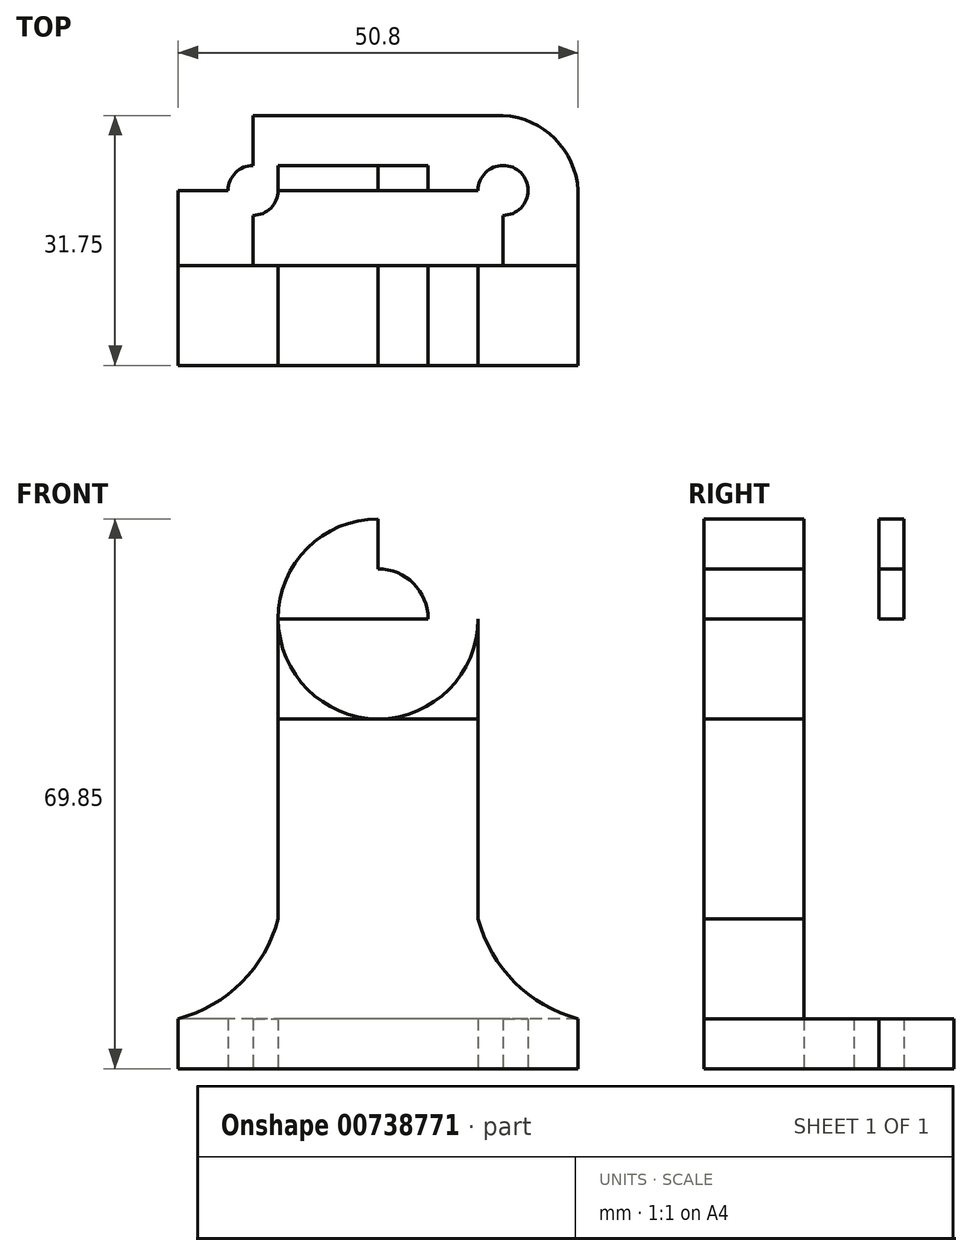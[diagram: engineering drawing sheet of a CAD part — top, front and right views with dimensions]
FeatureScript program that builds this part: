
annotation { "Feature Type Name" : "Feature", "Feature Type Description" : "" }
export const myFeature = defineFeature(function(context is Context, id is Id, definition is map)
    precondition{}
    {
        {
            var Q0;
            Q0=qCreatedBy(makeId("Right.planeOp"),FACE);
            var sketch = newSketch(context, id + "F0", { "sketchPlane" : qUnion([Q0])});
            skLineSegment(sketch, "E0", {"start": v(0, 0) * mm, "end": v(0, 69.85) * mm});
            skLineSegment(sketch, "E1", {"start": v(0, 69.85) * mm, "end": v(25.4, 69.85) * mm});
            skLineSegment(sketch, "E2", {"start": v(25.4, 69.85) * mm, "end": v(25.4, 44.45) * mm});
            skLineSegment(sketch, "E3", {"start": v(25.4, 44.45) * mm, "end": v(12.7, 44.45) * mm});
            skLineSegment(sketch, "E4", {"start": v(12.7, 44.45) * mm, "end": v(12.7, 6.35) * mm});
            skLineSegment(sketch, "E5", {"start": v(12.7, 6.35) * mm, "end": v(31.75, 6.35) * mm});
            skLineSegment(sketch, "E6", {"start": v(31.75, 6.35) * mm, "end": v(31.75, 0) * mm});
            skLineSegment(sketch, "E7", {"start": v(31.75, 0) * mm, "end": v(0, 0) * mm});
            skSolve(sketch);
        }
        {
            var Q0;
            Q0 = qSketchRegion(id + "F0", true);
            extrude(context, id + "F1", {"entities" : qUnion([Q0]), "depth" : 50.8 * mm, "offsetDistance" : 25.4 * mm});
        }
        {
            var Q0;
            Q0=qCreatedBy(makeId("Front.planeOp"),FACE);
            var sketch = newSketch(context, id + "F2", { "sketchPlane" : qUnion([Q0])});
            skLineSegment(sketch, "E8", {"start": v(38.1, 44.45) * mm, "end": v(38.1, 6.35) * mm});
            skLineSegment(sketch, "E9", {"start": v(12.7, 44.45) * mm, "end": v(12.7, 6.35) * mm});
            skLineSegment(sketch, "E10", {"start": v(50.8, 19.05) * mm, "end": v(0, 19.05) * mm});
            skArc(sketch, "E11", {"start": v(38.1, 19.05) * mm, "mid": v(42.73, 10.98) * mm, "end": v(50.8, 6.35) * mm});
            skArc(sketch, "E12", {"start": v(0, 6.35) * mm, "mid": v(8.07, 10.98) * mm, "end": v(12.7, 19.05) * mm});
            skLineSegment(sketch, "E13", {"start": v(38.1, 19.05) * mm, "end": v(38.1, 44.45) * mm});
            skLineSegment(sketch, "E14", {"start": v(38.1, 44.45) * mm, "end": v(50.8, 44.45) * mm});
            skLineSegment(sketch, "E15", {"start": v(50.8, 44.45) * mm, "end": v(50.8, 6.35) * mm});
            skLineSegment(sketch, "E16", {"start": v(12.7, 44.45) * mm, "end": v(0, 44.45) * mm});
            skLineSegment(sketch, "E17", {"start": v(0, 44.45) * mm, "end": v(0, 6.35) * mm});
            skLineSegment(sketch, "E18", {"start": v(38.1, 6.35) * mm, "end": v(38.1, 69.85) * mm});
            skLineSegment(sketch, "E19", {"start": v(38.1, 69.85) * mm, "end": v(50.8, 69.85) * mm});
            skLineSegment(sketch, "E20", {"start": v(50.8, 69.85) * mm, "end": v(50.8, 6.35) * mm});
            skLineSegment(sketch, "E21", {"start": v(12.7, 6.35) * mm, "end": v(12.7, 69.85) * mm});
            skLineSegment(sketch, "E22", {"start": v(12.7, 69.85) * mm, "end": v(0, 69.85) * mm});
            skLineSegment(sketch, "E23", {"start": v(0, 69.85) * mm, "end": v(0, 6.35) * mm});
            skSolve(sketch);
        }
        {
            var Q0;
            Q0 = qSketchRegion(id + "F2", true);
            extrude(context, id + "F3", {"entities" : qUnion([Q0]), "operationType" : NewBodyOperationType.REMOVE, "endBound" : BoundingType.THROUGH_ALL, "oppositeDirection" : true, "depth" : 25.4 * mm, "offsetDistance" : 25.4 * mm});
        }
        {
            var Q0;
            Q0=qCreatedBy(makeId("Front.planeOp"),FACE);
            var sketch = newSketch(context, id + "F4", { "sketchPlane" : qUnion([Q0])});
            skLineSegment(sketch, "E24", {"start": v(25.4, 69.85) * mm, "end": v(25.4, 44.45) * mm});
            skLineSegment(sketch, "E25", {"start": v(38, 57.15) * mm, "end": v(12.6, 57.15) * mm});
            skCircle(sketch, "E26", {"center": v(25.4, 57.15) * mm, "radius": 6.35 * mm});
            skCircle(sketch, "E27", {"center": v(25.4, 57.15) * mm, "radius": 12.7 * mm});
            skLineSegment(sketch, "E28", {"start": v(25.4, 69.85) * mm, "end": v(38.1, 69.85) * mm});
            skLineSegment(sketch, "E29", {"start": v(38.1, 69.85) * mm, "end": v(38.1, 44.45) * mm});
            skLineSegment(sketch, "E30", {"start": v(38.1, 44.45) * mm, "end": v(25.4, 44.45) * mm});
            skLineSegment(sketch, "E31", {"start": v(25.4, 44.45) * mm, "end": v(12.7, 44.45) * mm});
            skLineSegment(sketch, "E32", {"start": v(12.7, 44.45) * mm, "end": v(12.7, 69.85) * mm});
            skLineSegment(sketch, "E33", {"start": v(12.7, 69.85) * mm, "end": v(25.4, 69.85) * mm});
            skSolve(sketch);
        }
        {
            var Q0;
            {var subQ0=sQuery(id+"F4.wireOp",EDGE,"E28");Q0=makeQuery(id+"F4.imprint","IMPRINT",FACE,{"disambiguationData":[TD([[makeQuery(id+"F4.imprint","IMPRINT",EDGE,{"derivedFrom":subQ0}),-1.0]])]});}
            var Q1;
            {var subQ0=sQuery(id+"F4.wireOp",EDGE,"E33");Q1=makeQuery(id+"F4.imprint","IMPRINT",FACE,{"disambiguationData":[TD([[makeQuery(id+"F4.imprint","IMPRINT",EDGE,{"derivedFrom":subQ0}),-1.0]])]});}
            var Q2;
            {var subQ0=sQuery(id+"F4.wireOp",EDGE,"E31");Q2=makeQuery(id+"F4.imprint","IMPRINT",FACE,{"disambiguationData":[TD([[makeQuery(id+"F4.imprint","IMPRINT",EDGE,{"derivedFrom":subQ0}),-1.0]])]});}
            var Q3;
            {var subQ0=sQuery(id+"F4.wireOp",EDGE,"E30");Q3=makeQuery(id+"F4.imprint","IMPRINT",FACE,{"disambiguationData":[TD([[makeQuery(id+"F4.imprint","IMPRINT",EDGE,{"derivedFrom":subQ0}),-1.0]])]});}
            var Q4;
            {var subQ0=sQuery(id+"F4.wireOp",EDGE,"E25");var subQ1=sQuery(id+"F4.wireOp",EDGE,"E24");var subQ2=makeQuery(id+"F4.imprint","INTERSECT",VERTEX,{"derivedFrom":[subQ1,subQ0]});Q4=makeQuery(id+"F4.imprint","IMPRINT",FACE,{"disambiguationData":[TD([[makeQuery(id+"F4.imprint","IMPRINT",EDGE,{"disambiguationData":[TD([[subQ2,-1.0]])],"derivedFrom":subQ1}),-1.0]])]});}
            var Q5;
            {var subQ0=sQuery(id+"F4.wireOp",EDGE,"E25");var subQ1=sQuery(id+"F4.wireOp",EDGE,"E24");var subQ2=makeQuery(id+"F4.imprint","INTERSECT",VERTEX,{"derivedFrom":[subQ1,subQ0]});Q5=makeQuery(id+"F4.imprint","IMPRINT",FACE,{"disambiguationData":[TD([[makeQuery(id+"F4.imprint","IMPRINT",EDGE,{"disambiguationData":[TD([[subQ2,-1.0]])],"derivedFrom":subQ1}),1.0]])]});}
            var Q6;
            {var subQ0=sQuery(id+"F4.wireOp",EDGE,"E26");var subQ1=sQuery(id+"F4.wireOp",EDGE,"E24");var subQ2=makeQuery(id+"F4.imprint","INTERSECT",VERTEX,{"disambiguationData":[OD(0.0)],"derivedFrom":[subQ1,subQ0]});Q6=makeQuery(id+"F4.imprint","IMPRINT",FACE,{"disambiguationData":[TD([[makeQuery(id+"F4.imprint","IMPRINT",EDGE,{"disambiguationData":[TD([[subQ2,-1.0]])],"derivedFrom":subQ1}),1.0]])]});}
            var Q7;
            {var subQ0=sQuery(id+"F4.wireOp",EDGE,"E26");var subQ1=sQuery(id+"F4.wireOp",EDGE,"E24");var subQ2=makeQuery(id+"F4.imprint","INTERSECT",VERTEX,{"disambiguationData":[OD(0.0)],"derivedFrom":[subQ1,subQ0]});Q7=makeQuery(id+"F4.imprint","IMPRINT",FACE,{"disambiguationData":[TD([[makeQuery(id+"F4.imprint","IMPRINT",EDGE,{"disambiguationData":[TD([[subQ2,-1.0]])],"derivedFrom":subQ1}),-1.0]])]});}
            extrude(context, id + "F5", {"entities" : qUnion([Q0, Q1, Q2, Q3, Q4, Q5, Q6, Q7]), "operationType" : NewBodyOperationType.REMOVE, "endBound" : BoundingType.THROUGH_ALL, "oppositeDirection" : true, "depth" : 25.4 * mm, "offsetDistance" : 25.4 * mm});
        }
        {
            var Q0;
            Q0=qCreatedBy(makeId("Front.planeOp"),FACE);
            var sketch = newSketch(context, id + "F6", { "sketchPlane" : qUnion([Q0])});
            skLineSegment(sketch, "E34", {"start": v(12.71, 57.15) * mm, "end": v(38.11, 57.15) * mm});
            skLineSegment(sketch, "E35", {"start": v(12.71, 57.15) * mm, "end": v(12.71, 44.45) * mm});
            skLineSegment(sketch, "E36", {"start": v(12.71, 44.45) * mm, "end": v(38.11, 44.45) * mm});
            skLineSegment(sketch, "E37", {"start": v(38.11, 44.45) * mm, "end": v(38.11, 57.15) * mm});
            skArc(sketch, "E38", {"start": v(12.71, 57.15) * mm, "mid": v(16.43, 48.17) * mm, "end": v(25.41, 44.45) * mm});
            skArc(sketch, "E39", {"start": v(25.41, 44.45) * mm, "mid": v(34.4, 48.17) * mm, "end": v(38.11, 57.15) * mm});
            skSolve(sketch);
        }
        {
            var Q0;
            {var subQ0=sQuery(id+"F6.wireOp",EDGE,"E35");Q0=makeQuery(id+"F6.imprint","IMPRINT",FACE,{"disambiguationData":[TD([[makeQuery(id+"F6.imprint","IMPRINT",EDGE,{"derivedFrom":subQ0}),1.0]])]});}
            var Q1;
            {var subQ0=sQuery(id+"F6.wireOp",EDGE,"E37");Q1=makeQuery(id+"F6.imprint","IMPRINT",FACE,{"disambiguationData":[TD([[makeQuery(id+"F6.imprint","IMPRINT",EDGE,{"derivedFrom":subQ0}),1.0]])]});}
            extrude(context, id + "F7", {"entities" : qUnion([Q0, Q1]), "oppositeDirection" : true, "depth" : 12.7 * mm, "offsetDistance" : 25.4 * mm});
        }
        {
            var Q0;
            Q0=qCreatedBy(makeId("Top.planeOp"),FACE);
            var sketch = newSketch(context, id + "F8", { "sketchPlane" : qUnion([Q0])});
            skLineSegment(sketch, "E40", {"start": v(0, 12.7) * mm, "end": v(50.8, 12.7) * mm});
            skLineSegment(sketch, "E41", {"start": v(0, 22.23) * mm, "end": v(50.8, 22.23) * mm});
            skLineSegment(sketch, "E42", {"start": v(9.52, 31.75) * mm, "end": v(9.53, 12.7) * mm});
            skLineSegment(sketch, "E43", {"start": v(41.28, 12.7) * mm, "end": v(41.28, 31.75) * mm});
            skCircle(sketch, "E44", {"center": v(9.53, 22.23) * mm, "radius": 3.18 * mm});
            skCircle(sketch, "E45", {"center": v(41.28, 22.23) * mm, "radius": 3.18 * mm});
            skArc(sketch, "E46", {"start": v(9.52, 31.75) * mm, "mid": v(2.96, 28.8) * mm, "end": v(0, 22.23) * mm});
            skArc(sketch, "E47", {"start": v(50.8, 22.23) * mm, "mid": v(47.84, 28.8) * mm, "end": v(41.28, 31.75) * mm});
            skLineSegment(sketch, "E48", {"start": v(0, 22.23) * mm, "end": v(0, 31.75) * mm});
            skLineSegment(sketch, "E49", {"start": v(0, 31.75) * mm, "end": v(9.52, 31.75) * mm});
            skLineSegment(sketch, "E50", {"start": v(50.8, 22.23) * mm, "end": v(50.8, 31.75) * mm});
            skLineSegment(sketch, "E51", {"start": v(50.8, 31.75) * mm, "end": v(41.28, 31.75) * mm});
            skSolve(sketch);
        }
        {
            var Q0;
            {var subQ0=sQuery(id+"F8.wireOp",EDGE,"E44");var subQ1=sQuery(id+"F8.wireOp",EDGE,"E41");var subQ2=makeQuery(id+"F8.imprint","INTERSECT",VERTEX,{"disambiguationData":[OD(0.0)],"derivedFrom":[subQ1,subQ0]});Q0=makeQuery(id+"F8.imprint","IMPRINT",FACE,{"disambiguationData":[TD([[makeQuery(id+"F8.imprint","IMPRINT",EDGE,{"disambiguationData":[TD([[subQ2,-1.0]])],"derivedFrom":subQ1}),-1.0]])]});}
            var Q1;
            {var subQ0=sQuery(id+"F8.wireOp",EDGE,"E44");var subQ1=sQuery(id+"F8.wireOp",EDGE,"E41");var subQ2=makeQuery(id+"F8.imprint","INTERSECT",VERTEX,{"disambiguationData":[OD(1.0)],"derivedFrom":[subQ1,subQ0]});Q1=makeQuery(id+"F8.imprint","IMPRINT",FACE,{"disambiguationData":[TD([[makeQuery(id+"F8.imprint","IMPRINT",EDGE,{"disambiguationData":[TD([[subQ2,1.0]])],"derivedFrom":subQ1}),1.0]])]});}
            var Q2;
            {var subQ0=sQuery(id+"F8.wireOp",EDGE,"E45");var subQ1=sQuery(id+"F8.wireOp",EDGE,"E41");var subQ2=makeQuery(id+"F8.imprint","INTERSECT",VERTEX,{"disambiguationData":[OD(0.0)],"derivedFrom":[subQ1,subQ0]});Q2=makeQuery(id+"F8.imprint","IMPRINT",FACE,{"disambiguationData":[TD([[makeQuery(id+"F8.imprint","IMPRINT",EDGE,{"disambiguationData":[TD([[subQ2,-1.0]])],"derivedFrom":subQ1}),1.0]])]});}
            var Q3;
            {var subQ0=sQuery(id+"F8.wireOp",EDGE,"E45");var subQ1=sQuery(id+"F8.wireOp",EDGE,"E41");var subQ2=makeQuery(id+"F8.imprint","INTERSECT",VERTEX,{"disambiguationData":[OD(1.0)],"derivedFrom":[subQ1,subQ0]});Q3=makeQuery(id+"F8.imprint","IMPRINT",FACE,{"disambiguationData":[TD([[makeQuery(id+"F8.imprint","IMPRINT",EDGE,{"disambiguationData":[TD([[subQ2,1.0]])],"derivedFrom":subQ1}),-1.0]])]});}
            var Q4;
            {var subQ0=sQuery(id+"F8.wireOp",EDGE,"E44");var subQ1=sQuery(id+"F8.wireOp",EDGE,"E41");var subQ2=makeQuery(id+"F8.imprint","INTERSECT",VERTEX,{"disambiguationData":[OD(0.0)],"derivedFrom":[subQ1,subQ0]});Q4=makeQuery(id+"F8.imprint","IMPRINT",FACE,{"disambiguationData":[TD([[makeQuery(id+"F8.imprint","IMPRINT",EDGE,{"disambiguationData":[TD([[subQ2,-1.0]])],"derivedFrom":subQ1}),1.0]])]});}
            var Q5;
            {var subQ0=sQuery(id+"F8.wireOp",EDGE,"E44");var subQ1=sQuery(id+"F8.wireOp",EDGE,"E41");var subQ2=makeQuery(id+"F8.imprint","INTERSECT",VERTEX,{"disambiguationData":[OD(1.0)],"derivedFrom":[subQ1,subQ0]});Q5=makeQuery(id+"F8.imprint","IMPRINT",FACE,{"disambiguationData":[TD([[makeQuery(id+"F8.imprint","IMPRINT",EDGE,{"disambiguationData":[TD([[subQ2,1.0]])],"derivedFrom":subQ1}),-1.0]])]});}
            var Q6;
            {var subQ0=sQuery(id+"F8.wireOp",EDGE,"E45");var subQ1=sQuery(id+"F8.wireOp",EDGE,"E41");var subQ2=makeQuery(id+"F8.imprint","INTERSECT",VERTEX,{"disambiguationData":[OD(0.0)],"derivedFrom":[subQ1,subQ0]});Q6=makeQuery(id+"F8.imprint","IMPRINT",FACE,{"disambiguationData":[TD([[makeQuery(id+"F8.imprint","IMPRINT",EDGE,{"disambiguationData":[TD([[subQ2,-1.0]])],"derivedFrom":subQ1}),-1.0]])]});}
            var Q7;
            {var subQ0=sQuery(id+"F8.wireOp",EDGE,"E45");var subQ1=sQuery(id+"F8.wireOp",EDGE,"E41");var subQ2=makeQuery(id+"F8.imprint","INTERSECT",VERTEX,{"disambiguationData":[OD(1.0)],"derivedFrom":[subQ1,subQ0]});Q7=makeQuery(id+"F8.imprint","IMPRINT",FACE,{"disambiguationData":[TD([[makeQuery(id+"F8.imprint","IMPRINT",EDGE,{"disambiguationData":[TD([[subQ2,1.0]])],"derivedFrom":subQ1}),1.0]])]});}
            var Q8;
            Q8=makeQuery(id+"F8.imprint","IMPRINT",FACE,{"disambiguationData":[TD([[makeQuery(id+"F8.imprint","IMPRINT",EDGE,{"derivedFrom":sQuery(id+"F8.wireOp",EDGE,"E46")}),-1.0]])]});
            var Q9;
            Q9=makeQuery(id+"F8.imprint","IMPRINT",FACE,{"disambiguationData":[TD([[makeQuery(id+"F8.imprint","IMPRINT",EDGE,{"derivedFrom":sQuery(id+"F8.wireOp",EDGE,"E47")}),-1.0]])]});
            extrude(context, id + "F9", {"entities" : qUnion([Q0, Q1, Q2, Q3, Q4, Q5, Q6, Q7, Q8, Q9]), "operationType" : NewBodyOperationType.REMOVE, "endBound" : BoundingType.THROUGH_ALL, "depth" : 25.4 * mm, "offsetDistance" : 25.4 * mm});
        }
    });
